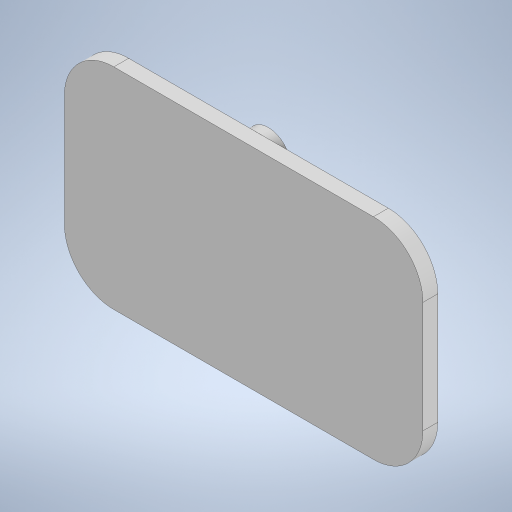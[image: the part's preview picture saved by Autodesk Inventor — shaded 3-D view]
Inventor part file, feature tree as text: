
AUTODESK INVENTOR PART (.ipt)
format: ipt  version: 2023 (Build 270158000, 158)  size: 229,376 bytes
history: native  units: mm
features: extrude x2, sketch x2, other x1, fillet x1, projected_geometry x1
ambient origin geometry x8: Origin, YZ Plane, XZ Plane, XY Plane, X Axis, Y Axis, Z Axis, Center Point
bodies: Body1 (feature_tree)
feature tree (7):
  other  "솔리드1"
  extrude  "돌출1"  Depth=72.5mm
  extrude  "돌출2"  Depth=42.5mm
  fillet  "모깎기1"  Radius=3.0mm
  sketch  "스케치1"
  sketch  "스케치2"
  projected_geometry  "투영된 루프1"
